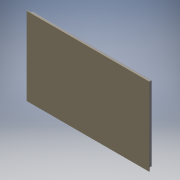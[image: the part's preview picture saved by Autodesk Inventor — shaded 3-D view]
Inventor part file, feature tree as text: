
AUTODESK INVENTOR PART (.ipt)
format: ipt  version: 2019 (Build 230136000, 136)  size: 99,840 bytes
history: native  units: mm
features: other x6, reference x4, extrude x2, sketch x2
ambient origin geometry x8: Origin, YZ Plane, XZ Plane, XY Plane, X Axis, Y Axis, Z Axis, Center Point
bodies: Solid1 (feature_tree)
feature tree (14):
  extrude  "Extrusion1"  Depth=861.06mm
  extrude  "Extrusion2"  Depth=25.4mm TaperAngle=0.0deg
  sketch  "Sketch1"  dims[d0=4.7625mm d1=0.0mm d2=861.06mm]
  sketch  "Sketch2"  dims[d3=549.275mm d4=25.4mm d5=0.0mm]
  reference  "Reference1"
  reference  "Reference2"
  reference  "Reference3"
  reference  "Reference4"
  parser-record x1  (decoder bookkeeping rows leaked as tree rows — omitted from the tree; the rows remain in map.json)
  other  "top_door.iam"
  other  "1515-S-BLACK_top_hatch_cross:1"
  other  "1515-S-BLACK_top_hatch_side:2"
  other  "1515-S-BLACK_top_hatch_side:1"
  other  "1515-S-BLACK_top_hatch_cross:2"
note: 1 file-system path scrubbed to <path> (originals preserved in map.json)
